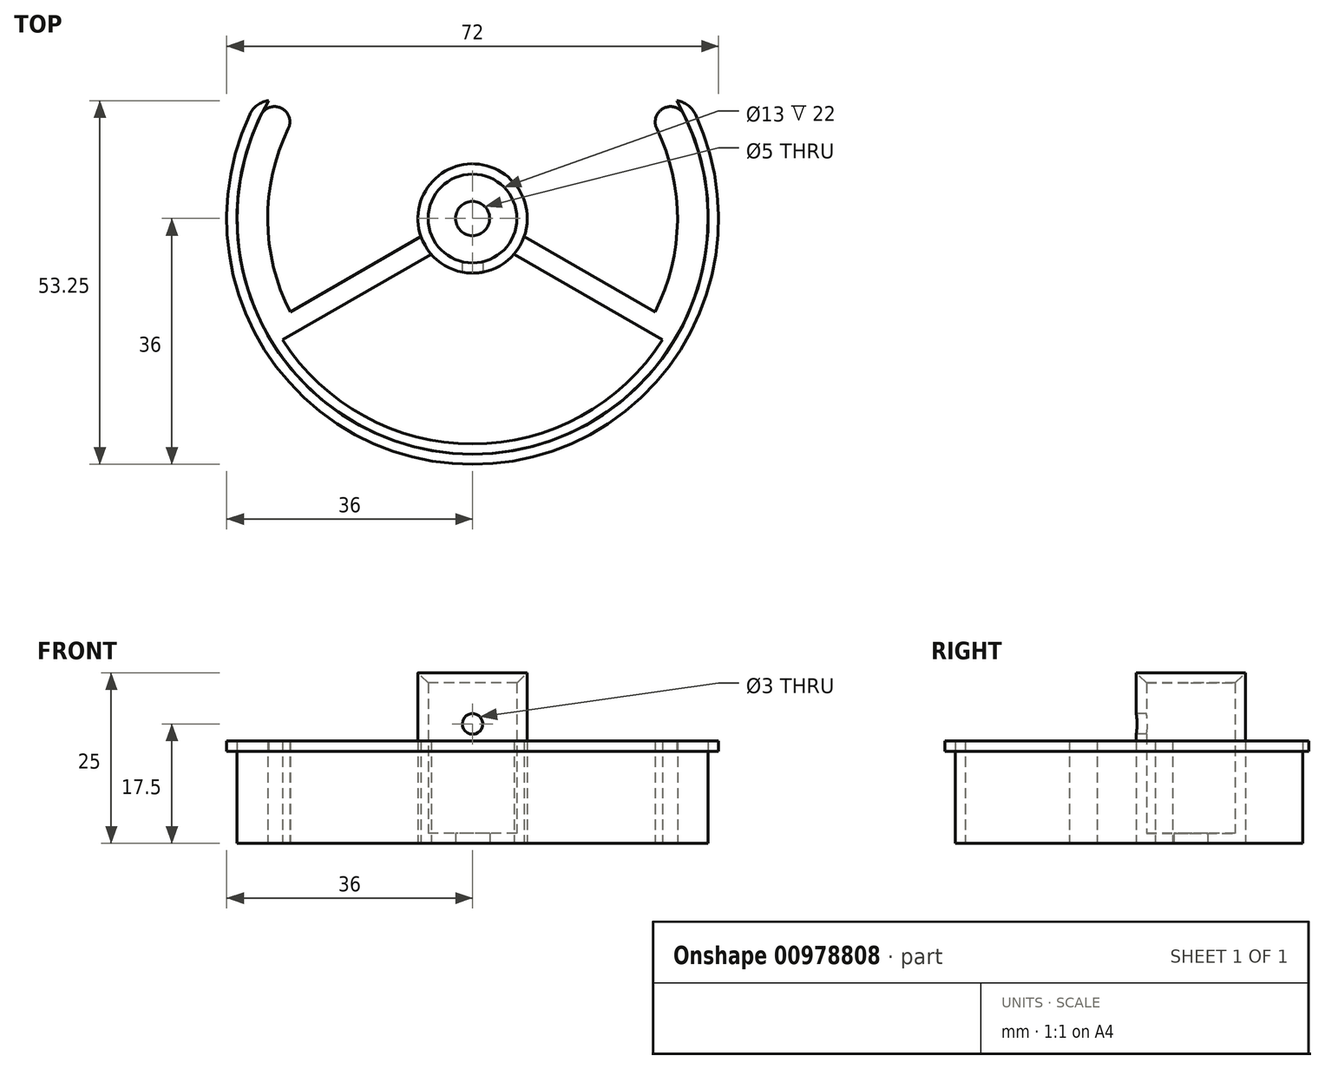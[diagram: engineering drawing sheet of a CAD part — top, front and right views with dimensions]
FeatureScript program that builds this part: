
annotation { "Feature Type Name" : "Feature", "Feature Type Description" : "" }
export const myFeature = defineFeature(function(context is Context, id is Id, definition is map)
    precondition{}
    {
        {
            assignVariable(context, id + "F0", {"name" : "wall", "anyValue" : 1.5});
        }
        {
            var Q0;
            Q0=qCreatedBy(makeId("Top.planeOp"),FACE);
            var sketch = newSketch(context, id + "F1", { "sketchPlane" : qUnion([Q0])});
            skArc(sketch, "E0", {"start": v(-29.88, 25.25) * mm, "mid": v(0, -26.5) * mm, "end": v(29.88, 25.25) * mm});
            skCircle(sketch, "E1", {"center": v(0, 8) * mm, "radius": 2.5 * mm});
            skCircle(sketch, "E2", {"center": v(0, 8) * mm, "radius": 8 * mm});
            skCircle(sketch, "E3", {"center": v(0, 8) * mm, "radius": 6.5 * mm});
            skArc(sketch, "E4", {"start": v(1.5, 40.97) * mm, "mid": v(0, 41) * mm, "end": v(-1.5, 40.97) * mm});
            skLineSegment(sketch, "E5", {"start": v(1.5, 40.97) * mm, "end": v(1.5, 15.86) * mm, "construction": true});
            skLineSegment(sketch, "E6.MirrorCS", {"start": v(-1.5, 40.97) * mm, "end": v(-1.5, 15.86) * mm, "construction": true});
            skLineSegment(sketch, "E7.1.0", {"start": v(-29.3, -7.18) * mm, "end": v(-7.56, 5.37) * mm});
            skLineSegment(sketch, "E7.1.1", {"start": v(-27.8, -9.78) * mm, "end": v(-6.06, 2.77) * mm});
            skLineSegment(sketch, "E7.2.0", {"start": v(27.8, -9.78) * mm, "end": v(6.06, 2.77) * mm});
            skLineSegment(sketch, "E7.2.1", {"start": v(29.3, -7.18) * mm, "end": v(7.56, 5.37) * mm});
            skLineSegment(sketch, "E8", {"start": v(1.5, 15.86) * mm, "end": v(-1.5, 15.86) * mm, "construction": true});
            skPoint(sketch, "E9", {"position": v(0, 15.86) * mm});
            skArc(sketch, "E10", {"start": v(26.7, -5.68) * mm, "mid": v(30, 8.75) * mm, "end": v(25.98, 23) * mm});
            skArc(sketch, "E11.trimOffspring", {"start": v(-29.3, -7.18) * mm, "mid": v(0, -25) * mm, "end": v(29.3, -7.18) * mm});
            skLineSegment(sketch, "E12", {"start": v(-29.88, 25.25) * mm, "end": v(-25.98, 23) * mm});
            skLineSegment(sketch, "E13.MirrorCS", {"start": v(29.88, 25.25) * mm, "end": v(25.98, 23) * mm});
            skArc(sketch, "E14.trimOffspring", {"start": v(-25.98, 23) * mm, "mid": v(-30, 8.75) * mm, "end": v(-26.7, -5.68) * mm});
            skArc(sketch, "E15.trimOffspring", {"start": v(1.5, 37.96) * mm, "mid": v(0, 38) * mm, "end": v(-1.5, 37.96) * mm});
            skLineSegment(sketch, "E16", {"start": v(0, 8) * mm, "end": v(-31.18, 26) * mm, "construction": true});
            skArc(sketch, "E17", {"start": v(-31.18, 26) * mm, "mid": v(0, -28) * mm, "end": v(31.18, 26) * mm});
            skLineSegment(sketch, "E18", {"start": v(31.18, 26) * mm, "end": v(29.88, 25.25) * mm});
            skLineSegment(sketch, "E19", {"start": v(-29.88, 25.25) * mm, "end": v(-31.18, 26) * mm});
            skSolve(sketch);
        }
        {
            var Q0;
            Q0=makeQuery(id+"F1.imprint","IMPRINT",FACE,{"disambiguationData":[TD([[makeQuery(id+"F1.imprint","IMPRINT",EDGE,{"derivedFrom":sQuery(id+"F1.wireOp",EDGE,"E3")}),-1.0]])]});
            extrude(context, id + "F2", {"entities" : qUnion([Q0]), "depth" : 25 * mm, "offsetDistance" : 25 * mm});
        }
        {
            var Q0;
            Q0=makeQuery(id+"F1.imprint","IMPRINT",FACE,{"disambiguationData":[TD([[makeQuery(id+"F1.imprint","IMPRINT",EDGE,{"derivedFrom":sQuery(id+"F1.wireOp",EDGE,"E0")}),1.0]])]});
            var Q1;
            {var subQ0=sQuery(id+"F1.wireOp",EDGE,"E7.1.0");Q1=makeQuery(id+"F1.imprint","IMPRINT",FACE,{"disambiguationData":[TD([[makeQuery(id+"F1.imprint","IMPRINT",EDGE,{"derivedFrom":subQ0}),-1.0]])]});}
            var Q2;
            {var subQ0=sQuery(id+"F1.wireOp",EDGE,"E7.2.0");Q2=makeQuery(id+"F1.imprint","IMPRINT",FACE,{"disambiguationData":[TD([[makeQuery(id+"F1.imprint","IMPRINT",EDGE,{"derivedFrom":subQ0}),-1.0]])]});}
            var Q3;
            {var subQ0=sQuery(id+"F1.wireOp",EDGE,"E5");Q3=makeQuery(id+"F1.imprint","IMPRINT",FACE,{"disambiguationData":[TD([[makeQuery(id+"F1.imprint","IMPRINT",EDGE,{"derivedFrom":subQ0}),-1.0]])]});}
            extrude(context, id + "F3", {"entities" : qUnion([Q0, Q1, Q2, Q3]), "operationType" : NewBodyOperationType.ADD, "depth" : 15 * mm, "offsetDistance" : 25 * mm});
        }
        {
            var Q0;
            Q0=makeQuery(id+"F1.imprint","IMPRINT",FACE,{"disambiguationData":[TD([[makeQuery(id+"F1.imprint","IMPRINT",EDGE,{"derivedFrom":sQuery(id+"F1.wireOp",EDGE,"E0")}),-1.0]])]});
            extrude(context, id + "F4", {"entities" : qUnion([Q0]), "depth" : (getVariable(context, 'wall')) * mm, "offsetDistance" : 25 * mm});
        }
        {
            var Q0;
            Q0=makeQuery(id+"F4.opExtrude","SWEPT_BODY",BODY,{"disambiguationData":[OSD([sQuery(id+"F1.wireOp",EDGE,"E0"),sQuery(id+"F1.wireOp",EDGE,"E17"),sQuery(id+"F1.wireOp",EDGE,"E18"),sQuery(id+"F1.wireOp",EDGE,"E19")])]});
            transform(context, id + "F5", {"entities" : qUnion([Q0]), "transformType" : TransformType.TRANSLATION_3D, "dx" : 0 * mm, "dy" : 0 * mm, "dz" : (15 - getVariable(context, 'wall')) * mm, "makeCopy" : false});
        }
        {
            var Q0;
            Q0=makeQuery(id+"F1.imprint","IMPRINT",FACE,{"disambiguationData":[TD([[makeQuery(id+"F1.imprint","IMPRINT",EDGE,{"derivedFrom":sQuery(id+"F1.wireOp",EDGE,"E1")}),-1.0]])]});
            extrude(context, id + "F6", {"entities" : qUnion([Q0]), "operationType" : NewBodyOperationType.ADD, "depth" : (getVariable(context, 'wall')) * mm, "offsetDistance" : 25 * mm});
        }
        {
            var Q0;
            Q0=qCreatedBy(makeId("Front.planeOp"),FACE);
            var sketch = newSketch(context, id + "F7", { "sketchPlane" : qUnion([Q0])});
            skCircle(sketch, "E20", {"center": v(0, 17.5) * mm, "radius": 1.5 * mm});
            skLineSegment(sketch, "E21", {"start": v(0, 17.5) * mm, "end": v(0, 25) * mm, "construction": true});
            skSolve(sketch);
        }
        {
            var Q0;
            Q0=makeQuery(id+"F7.imprint","IMPRINT",FACE,{"disambiguationData":[TD([[makeQuery(id+"F7.imprint","IMPRINT",EDGE,{"derivedFrom":sQuery(id+"F7.wireOp",EDGE,"E20")}),1.0]])]});
            var Q1;
            Q1=makeQuery(id+"F2.opExtrude","SWEPT_BODY",BODY,{"disambiguationData":[OSD([sQuery(id+"F1.wireOp",EDGE,"E2"),sQuery(id+"F1.wireOp",EDGE,"E3")])]});
            extrude(context, id + "F8", {"entities" : qUnion([Q0]), "operationType" : NewBodyOperationType.REMOVE, "oppositeDirection" : true, "depth" : (getVariable(context, 'wall') * 2) * mm, "endBoundEntityBody" : qUnion([Q1]), "offsetDistance" : 25 * mm});
        }
        {
            var Q0;
            Q0=makeQuery(id+"F3.opExtrude","SWEPT_EDGE",EDGE,{"disambiguationData":[OSD([sQuery(id+"F1.wireOp",EDGE,"E0"),sQuery(id+"F1.wireOp",EDGE,"E12")])]});
            var Q1;
            Q1=makeQuery(id+"F3.opExtrude","SWEPT_EDGE",EDGE,{"disambiguationData":[OSD([sQuery(id+"F1.wireOp",EDGE,"E12"),sQuery(id+"F1.wireOp",EDGE,"E14.trimOffspring")])]});
            var Q2;
            Q2=makeQuery(id+"F3.opExtrude","SWEPT_EDGE",EDGE,{"disambiguationData":[OSD([sQuery(id+"F1.wireOp",EDGE,"E10"),sQuery(id+"F1.wireOp",EDGE,"E13.MirrorCS")])]});
            var Q3;
            Q3=makeQuery(id+"F3.opExtrude","SWEPT_EDGE",EDGE,{"disambiguationData":[OSD([sQuery(id+"F1.wireOp",EDGE,"E0"),sQuery(id+"F1.wireOp",EDGE,"E13.MirrorCS")])]});
            fillet(context, id + "F9", {"entities" : qUnion([Q0, Q1, Q2, Q3]), "radius" : (getVariable(context, 'wall') * 3 / 2) * mm, "tangentPropagation" : true, "allowEdgeOverflow" : false});
        }
        {
            var Q0;
            Q0=makeQuery(id+"F2.opExtrude","CAP_EDGE",EDGE,{"disambiguationData":[OSD([sQuery(id+"F1.wireOp",EDGE,"E3")])],"isStart":false});
            chamfer(context, id + "F10", {"entities" : qUnion([Q0]), "width" : (getVariable(context, 'wall')) * mm, "tangentPropagation" : true});
        }
        {
            var Q0;
            Q0=makeQuery(id+"F4.opExtrude","SWEPT_EDGE",EDGE,{"disambiguationData":[OSD([sQuery(id+"F1.wireOp",EDGE,"E17"),sQuery(id+"F1.wireOp",EDGE,"E19")])]});
            var Q1;
            Q1=makeQuery(id+"F4.opExtrude","SWEPT_EDGE",EDGE,{"disambiguationData":[OSD([sQuery(id+"F1.wireOp",EDGE,"E17"),sQuery(id+"F1.wireOp",EDGE,"E18")])]});
            fillet(context, id + "F11", {"entities" : qUnion([Q0, Q1]), "radius" : 3.5 * mm, "tangentPropagation" : true, "allowEdgeOverflow" : false});
        }
    });
